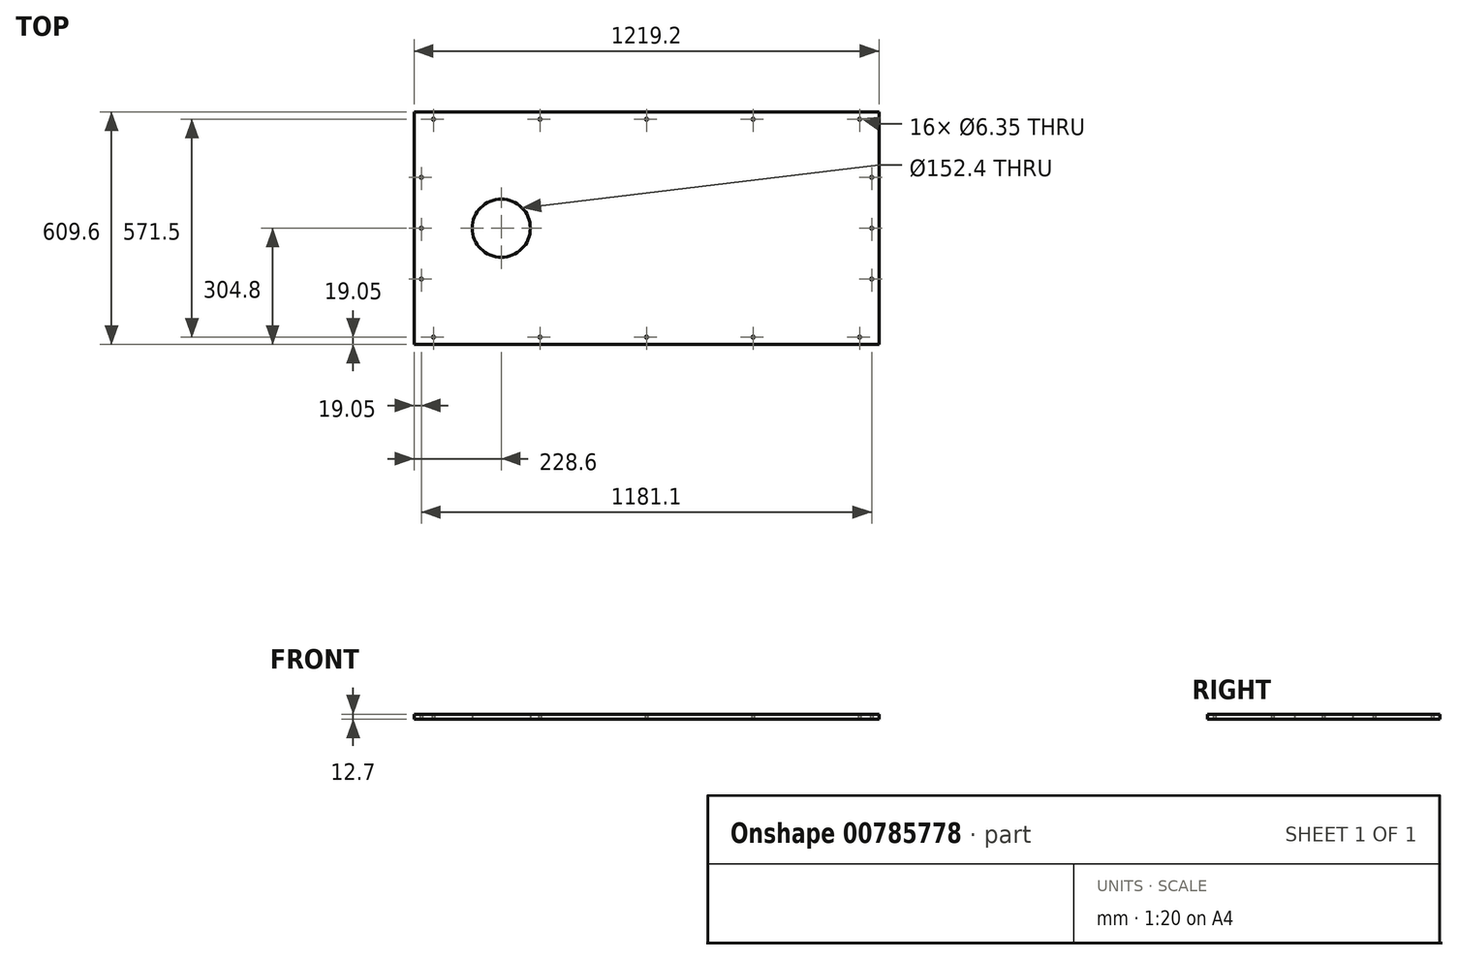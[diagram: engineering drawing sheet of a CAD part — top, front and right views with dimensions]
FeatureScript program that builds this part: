
annotation { "Feature Type Name" : "Feature", "Feature Type Description" : "" }
export const myFeature = defineFeature(function(context is Context, id is Id, definition is map)
    precondition{}
    {
        {
            var Q0;
            Q0=qCreatedBy(makeId("Top.planeOp"),FACE);
            var sketch = newSketch(context, id + "F0", { "sketchPlane" : qUnion([Q0])});
            skLineSegment(sketch, "E0.bottom", {"start": v(609.6, -304.8) * mm, "end": v(-609.6, -304.8) * mm});
            skLineSegment(sketch, "E0.top", {"start": v(609.6, 304.8) * mm, "end": v(-609.6, 304.8) * mm});
            skLineSegment(sketch, "E0.left", {"start": v(-609.6, -304.8) * mm, "end": v(-609.6, 304.8) * mm});
            skLineSegment(sketch, "E0.right", {"start": v(609.6, -304.8) * mm, "end": v(609.6, 304.8) * mm});
            skPoint(sketch, "E0.middle", {"position": v(0, 0) * mm});
            skLineSegment(sketch, "E1", {"start": v(-381, -304.8) * mm, "end": v(-381, 304.8) * mm, "construction": true});
            skLineSegment(sketch, "E2", {"start": v(-381, 0) * mm, "end": v(-609.6, 0) * mm, "construction": true});
            skLineSegment(sketch, "E3", {"start": v(-609.6, 285.75) * mm, "end": v(609.6, 285.75) * mm, "construction": true});
            skPoint(sketch, "E4", {"position": v(-558.8, 285.75) * mm});
            skPoint(sketch, "E5", {"position": v(-279.4, 285.75) * mm});
            skPoint(sketch, "E6", {"position": v(0, 285.75) * mm});
            skPoint(sketch, "E7", {"position": v(279.4, 285.75) * mm});
            skPoint(sketch, "E8", {"position": v(558.8, 285.75) * mm});
            skPoint(sketch, "E9.MirrorP", {"position": v(-558.8, -285.75) * mm});
            skPoint(sketch, "E10.MirrorP", {"position": v(-279.4, -285.75) * mm});
            skPoint(sketch, "E11.MirrorP", {"position": v(0, -285.75) * mm});
            skPoint(sketch, "E12.MirrorP", {"position": v(279.4, -285.75) * mm});
            skPoint(sketch, "E13.MirrorP", {"position": v(558.8, -285.75) * mm});
            skLineSegment(sketch, "E14", {"start": v(-590.55, 285.75) * mm, "end": v(-590.55, -304.8) * mm, "construction": true});
            skPoint(sketch, "E15", {"position": v(-590.55, 133.35) * mm});
            skPoint(sketch, "E16", {"position": v(-590.55, 0) * mm});
            skPoint(sketch, "E17", {"position": v(-590.55, -133.35) * mm});
            skLineSegment(sketch, "E18", {"start": v(0, 142.58) * mm, "end": v(0, -128.99) * mm, "construction": true});
            skPoint(sketch, "E19.MirrorP", {"position": v(590.55, 133.35) * mm});
            skPoint(sketch, "E20.MirrorP", {"position": v(590.55, 0) * mm});
            skPoint(sketch, "E21.MirrorP", {"position": v(590.55, -133.35) * mm});
            skSolve(sketch);
        }
        {
            var Q0;
            Q0=makeQuery(id+"F0.imprint","IMPRINT",FACE,{"disambiguationData":[TD([[makeQuery(id+"F0.imprint","IMPRINT",EDGE,{"derivedFrom":sQuery(id+"F0.wireOp",EDGE,"E0.bottom")}),-1.0]])]});
            extrude(context, id + "F1", {"entities" : qUnion([Q0]), "depth" : 12.7 * mm, "offsetDistance" : 25.4 * mm});
        }
        {
            var Q0;
            Q0=sQuery(id+"F0.wireOp",VERTEX,"E2.start");
            var Q1;
            Q1=makeQuery(id+"F1.opExtrude","SWEPT_BODY",BODY,{"disambiguationData":[OSD([sQuery(id+"F0.wireOp",EDGE,"E0.bottom"),sQuery(id+"F0.wireOp",EDGE,"E0.top"),sQuery(id+"F0.wireOp",EDGE,"E0.left"),sQuery(id+"F0.wireOp",EDGE,"E0.right")])]});
            hole(context, id + "F2", {"style" : HoleStyle.SIMPLE, "endStyle" : HoleEndStyle.THROUGH, "oppositeDirection" : true, "holeDiameter" : 152.4 * mm, "majorDiameter" : 6.35 * mm, "isTappedThrough" : true, "tappedDepth" : 12.7 * mm, "tapClearance" : 3, "locations" : qUnion([Q0]), "scope" : qUnion([Q1])});
        }
        {
            var Q0;
            Q0=sQuery(id+"F0.wireOp",VERTEX,"E4");
            var Q1;
            Q1=sQuery(id+"F0.wireOp",VERTEX,"E5");
            var Q2;
            Q2=sQuery(id+"F0.wireOp",VERTEX,"E6");
            var Q3;
            Q3=sQuery(id+"F0.wireOp",VERTEX,"E7");
            var Q4;
            Q4=sQuery(id+"F0.wireOp",VERTEX,"E8");
            var Q5;
            Q5=sQuery(id+"F0.wireOp",VERTEX,"E13.MirrorP");
            var Q6;
            Q6=sQuery(id+"F0.wireOp",VERTEX,"E12.MirrorP");
            var Q7;
            Q7=sQuery(id+"F0.wireOp",VERTEX,"E11.MirrorP");
            var Q8;
            Q8=sQuery(id+"F0.wireOp",VERTEX,"E10.MirrorP");
            var Q9;
            Q9=sQuery(id+"F0.wireOp",VERTEX,"E9.MirrorP");
            var Q10;
            Q10=sQuery(id+"F0.wireOp",VERTEX,"E15");
            var Q11;
            Q11=sQuery(id+"F0.wireOp",VERTEX,"E16");
            var Q12;
            Q12=sQuery(id+"F0.wireOp",VERTEX,"E17");
            var Q13;
            Q13=sQuery(id+"F0.wireOp",VERTEX,"E19.MirrorP");
            var Q14;
            Q14=sQuery(id+"F0.wireOp",VERTEX,"E20.MirrorP");
            var Q15;
            Q15=sQuery(id+"F0.wireOp",VERTEX,"E21.MirrorP");
            var Q16;
            Q16=makeQuery(id+"F1.opExtrude","SWEPT_BODY",BODY,{"disambiguationData":[OSD([sQuery(id+"F0.wireOp",EDGE,"E0.bottom"),sQuery(id+"F0.wireOp",EDGE,"E0.top"),sQuery(id+"F0.wireOp",EDGE,"E0.left"),sQuery(id+"F0.wireOp",EDGE,"E0.right")])]});
            hole(context, id + "F3", {"style" : HoleStyle.SIMPLE, "endStyle" : HoleEndStyle.THROUGH, "oppositeDirection" : true, "holeDiameter" : 6.35 * mm, "majorDiameter" : 6.35 * mm, "isTappedThrough" : true, "tappedDepth" : 12.7 * mm, "tapClearance" : 3, "locations" : qUnion([Q0, Q1, Q2, Q3, Q4, Q5, Q6, Q7, Q8, Q9, Q10, Q11, Q12, Q13, Q14, Q15]), "scope" : qUnion([Q16])});
        }
    });
